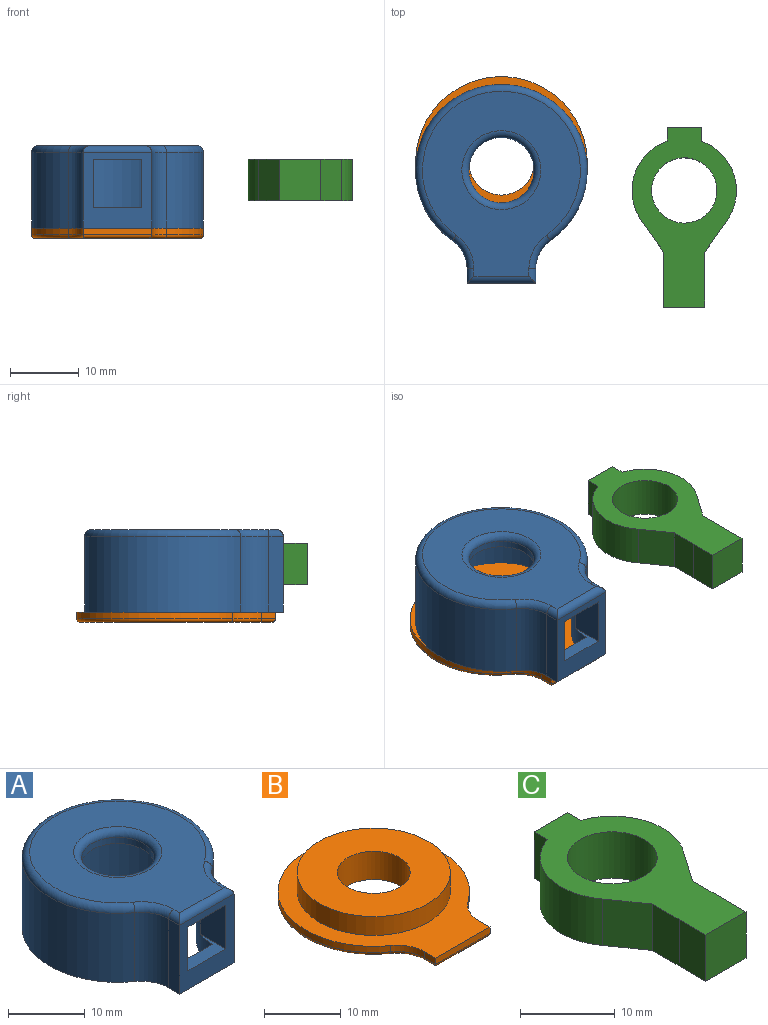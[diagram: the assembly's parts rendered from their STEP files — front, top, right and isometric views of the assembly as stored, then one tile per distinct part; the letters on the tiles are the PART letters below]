
ASSEMBLY  parts=3 mates=3
PART A: 26 faces, bbox 27.1x30x12 mm
  f0: plane 11x10mm, normal (0,-1,0), area 61mm2, adj f1,f3,f5,f12,f16,f17,f18,f22
  f1: plane 11x2.1mm, normal (1,0,0), area 23mm2, adj f0,f5,f6,f20
  f2: cylinder r=12.5mm len=25mm, axis (0,0,-1), area 696.7mm2, adj f5,f6,f7,f23
  f3: plane 11x2.1mm, normal (-1,0,0), area 23mm2, adj f0,f5,f7,f24
  f4: plane 26.96x23mm, normal (0,0,1), area 348.9mm2, adj f19,f20,f21,f22,f23,f24,f25
  f5: plane 28.96x25mm, normal (0,0,-1), area 160mm2, adj f0,f1,f2,f3,f6,f7,f8,f9
  f6: cylinder r=5mm len=11mm, axis (0,0,-1), area 52.9mm2, adj f1,f2,f5,f21
  f7: cylinder r=5mm len=11mm, axis (0,0,-1), area 52.9mm2, adj f2,f3,f5,f25
  f8: plane 3x0.1mm, normal (-1,0,0), area 0.3mm2, adj f5,f11,f13,f17
  f9: cylinder r=10.5mm len=21mm, axis (0,0,-1), area 532mm2, adj f5,f12,f13,f14
  f10: plane 3x0.1mm, normal (1,0,0), area 0.3mm2, adj f5,f11,f14,f17
  f11: plane 6x3mm, normal (0,1,0), area 18mm2, adj f5,f8,f10,f17
  f12: plane 26.96x21mm, normal (0,0,-1), area 321.3mm2, adj f0,f9,f13,f14,f15,f16,f18
  f13: cylinder r=7mm len=10mm, axis (0,0,-1), area 48.7mm2, adj f5,f8,f9,f12,f17,f18
  f14: cylinder r=7mm len=10mm, axis (0,0,-1), area 48.7mm2, adj f5,f9,f10,f12,f16,f17
  f15: cylinder r=4.75mm len=9.5mm, axis (0,0,1), area 29.8mm2, adj f12,f19
  f16: plane 7x4.69mm, normal (1,0,0), area 32.9mm2, adj f0,f12,f14,f17
  f17: plane 7x4.69mm, normal (0,0,1), area 15.8mm2, adj f0,f8,f10,f11,f13,f14,f16,f18
  f18: plane 7x4.69mm, normal (-1,0,0), area 32.9mm2, adj f0,f12,f13,f17
  f19: torus R=5.75mm, axis (0,0,1), area 50.5mm2, adj f4,f15
  f20: cylinder r=1mm len=2.1mm, axis (0,-1,0), area 2.7mm2, adj f1,f4,f21,f22
  f21: torus R=6mm, axis (0,0,1), area 8.1mm2, adj f4,f6,f20,f23
  f22: cylinder r=1mm len=10mm, axis (-1,0,0), area 14.6mm2, adj f0,f4,f20,f24
  f23: torus R=11.5mm, axis (0,0,1), area 96.6mm2, adj f2,f4,f21,f25
  f24: cylinder r=1mm len=2.1mm, axis (0,1,0), area 2.7mm2, adj f3,f4,f22,f25
  f25: torus R=6mm, axis (0,0,1), area 8.1mm2, adj f4,f7,f23,f24
PART B: 17 faces, bbox 27.1x30x4.5 mm
  f0: plane 2.1x1mm, normal (1,0,0), area 2.1mm2, adj f3,f4,f6,f8
  f1: cylinder r=12.5mm len=25mm, axis (0,0,-1), area 63.3mm2, adj f4,f6,f7,f12
  f2: plane 2.1x1mm, normal (-1,0,0), area 2.1mm2, adj f3,f4,f7,f11
  f3: plane 10x1mm, normal (0,-1,0), area 10mm2, adj f0,f2,f4,f9
  f4: plane 28.96x25mm, normal (0,0,1), area 222.2mm2, adj f0,f1,f2,f3,f6,f7,f15
  f5: plane 27.96x24mm, normal (0,0,-1), area 422.8mm2, adj f8,f9,f10,f11,f12,f13,f14
  f6: cylinder r=5mm len=4.1mm, axis (0,0,-1), area 4.8mm2, adj f0,f1,f4,f10
  f7: cylinder r=5mm len=4.1mm, axis (0,0,-1), area 4.8mm2, adj f1,f2,f4,f13
  f8: cylinder r=0.5mm len=2.1mm, axis (0,1,0), area 1.5mm2, adj f0,f5,f9,f10
  f9: cylinder r=0.5mm len=10mm, axis (1,0,0), area 7.6mm2, adj f3,f5,f8,f11
  f10: torus R=5.5mm, axis (0,0,1), area 3.9mm2, adj f5,f6,f8,f12
  f11: cylinder r=0.5mm len=2.1mm, axis (0,-1,0), area 1.5mm2, adj f2,f5,f9,f13
  f12: torus R=12mm, axis (0,0,1), area 49mm2, adj f1,f5,f10,f13
  f13: torus R=5.5mm, axis (0,0,1), area 3.9mm2, adj f5,f7,f11,f12
  f14: cylinder r=4.75mm len=9.5mm, axis (0,0,1), area 134.3mm2, adj f5,f16
  f15: cylinder r=10mm len=20mm, axis (0,0,-1), area 188.5mm2, adj f4,f16
  f16: plane 20x20mm, normal (0,0,1), area 243.3mm2, adj f14,f15
PART C: 20 faces, bbox 15.2x26.2x6 mm
  f0: plane 6x5mm, normal (0,1,0), area 17.8mm2, adj f10,f11,f13,f14,f15,f16,f17,f18
  f1: cylinder r=7.61mm len=11.81mm, axis (0,0,-1), area 86.2mm2, adj f2,f10,f11,f13
  f2: plane 6x4.37mm, normal (-0.82,-0.57,0), area 32mm2, adj f1,f3,f10,f11
  f3: plane 6x4mm, normal (-1,0,0), area 24mm2, adj f2,f4,f10,f11
  f4: plane 6x4mm, normal (-1,0,0), area 24mm2, adj f3,f5,f10,f11
  f5: plane 6x6mm, normal (0,-1,0), area 36mm2, adj f4,f6,f10,f11
  f6: plane 6x4mm, normal (1,0,0), area 24mm2, adj f5,f7,f10,f11
  f7: plane 6x4mm, normal (1,0,0), area 24mm2, adj f6,f8,f10,f11
  f8: plane 6x4.37mm, normal (0.82,-0.57,0), area 32mm2, adj f7,f9,f10,f11
  f9: cylinder r=7.61mm len=11.81mm, axis (0,0,-1), area 86.2mm2, adj f8,f10,f11,f14
  f10: plane 26.17x15.22mm, normal (0,0,1), area 181.9mm2, adj f0,f1,f2,f3,f4,f5,f6,f7
  f11: plane 26.17x15.22mm, normal (0,0,-1), area 181.9mm2, adj f0,f1,f2,f3,f4,f5,f6,f7
  f12: cylinder r=4.75mm len=9.5mm, axis (0,0,1), area 179.1mm2, adj f10,f11
  f13: plane 6x2mm, normal (-1,0,0), area 12mm2, adj f0,f1,f10,f11
  f14: plane 6x2mm, normal (1,0,0), area 12mm2, adj f0,f9,f10,f11
  f15: plane 3.5x0.5mm, normal (0,0,-1), area 1.8mm2, adj f0,f16,f18,f19
  f16: plane 3.5x0.5mm, normal (-1,0,0), area 1.8mm2, adj f0,f15,f17,f19
  f17: plane 3.5x0.5mm, normal (0,0,1), area 1.8mm2, adj f0,f16,f18,f19
  f18: plane 3.5x0.5mm, normal (1,0,0), area 1.8mm2, adj f0,f15,f17,f19
  f19: plane 3.5x3.5mm, normal (0,1,0), area 12.2mm2, adj f15,f16,f17,f18
PLACE A t=(-11.49,27.63,-15.21)mm
PLACE B t=(-11.49,15.48,-16.71)mm
PLACE C t=(15.13,12.31,-11.21)mm
MATE parallel B.f1 <-> A.f2  axis (0,0,1) through (-11.49,28.77,-15.21)mm
MATE planar B.f4 <-> A.f5  axis (0,0,1) through (-11.49,25.88,-15.21)mm
MATE planar C.f9 <-> A.f15  axis (0,0,1) through (15.13,24.68,-5.21)mm
